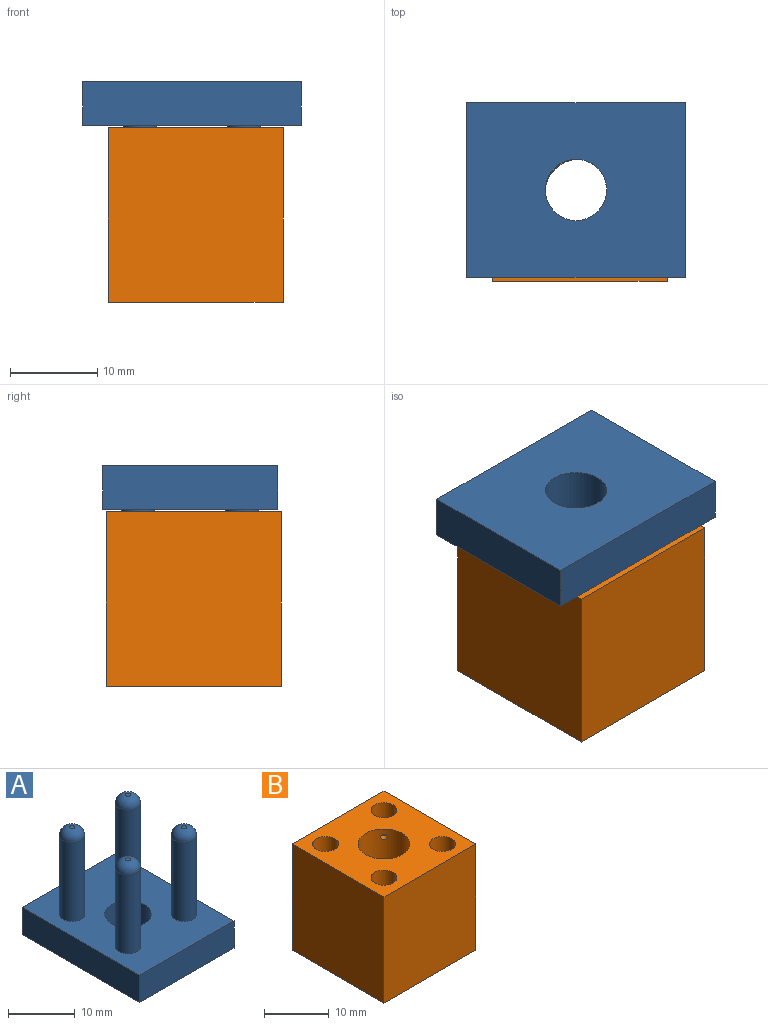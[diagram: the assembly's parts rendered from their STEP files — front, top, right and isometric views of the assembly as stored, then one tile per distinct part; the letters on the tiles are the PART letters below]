
ASSEMBLY  parts=2 mates=1
PART A: 19 faces, bbox 20x25x21 mm
  f0: plane 20x5mm, normal (0,1,0), area 100mm2, adj f1,f4,f5,f6
  f1: plane 25x5mm, normal (-1,0,0), area 125mm2, adj f0,f2,f5,f6
  f2: plane 20x5mm, normal (0,-1,0), area 100mm2, adj f1,f4,f5,f6
  f3: cylinder r=3.5mm len=7mm, axis (0,0,1), area 110mm2, adj f5,f6
  f4: plane 25x5mm, normal (1,0,0), area 125mm2, adj f0,f2,f5,f6
  f5: plane 25x20mm, normal (0,0,-1), area 461.5mm2, adj f0,f1,f2,f3,f4
  f6: plane 25x20mm, normal (0,0,1), area 416.2mm2, adj f0,f1,f2,f3,f4,f7,f9,f11
  f7: cylinder r=1.9mm len=14.5mm, axis (0,0,-1), area 173.1mm2, adj f6,f17
  f8: plane 0.8x0.8mm, normal (0,0,1), area 0.5mm2, adj f17
  f9: cylinder r=1.9mm len=14.5mm, axis (0,0,-1), area 173.1mm2, adj f6,f18
  f10: plane 0.8x0.8mm, normal (0,0,1), area 0.5mm2, adj f18
  f11: cylinder r=1.9mm len=14.5mm, axis (0,0,-1), area 173.1mm2, adj f6,f15
  f12: plane 0.8x0.8mm, normal (0,0,1), area 0.5mm2, adj f15
  f13: cylinder r=1.9mm len=14.5mm, axis (0,0,-1), area 173.1mm2, adj f6,f16
  f14: plane 0.8x0.8mm, normal (0,0,1), area 0.5mm2, adj f16
  f15: torus R=0.4mm, axis (0,0,1), area 20.1mm2, adj f11,f12
  f16: torus R=0.4mm, axis (0,0,1), area 20.1mm2, adj f13,f14
  f17: torus R=0.4mm, axis (0,0,1), area 20.1mm2, adj f7,f8
  f18: torus R=0.4mm, axis (0,0,1), area 20.1mm2, adj f9,f10
PART B: 61 faces, bbox 20x20x20 mm
  f0: plane 0.35x0.35mm, normal (0,0,1), area 0mm2, adj f1,f2
  f1: cylinder r=0.5mm len=3.54mm, axis (0.71,0.71,0), area 10.7mm2, adj f0,f2,f3,f4,f5
  f2: cylinder r=0.5mm len=16.75mm, axis (0,0,1), area 51.3mm2, adj f0,f1,f3,f6,f7
  f3: plane 0.35x0.35mm, normal (0,0,1), area 0mm2, adj f1,f2
  f4: plane 1x0.71mm, normal (0.71,0.71,0), area 0.8mm2, adj f1
  f5: cylinder r=0.5mm len=1mm, axis (0,0,1), area 1mm2, adj f1
  f6: cylinder r=0.5mm len=0.71mm, axis (-0.71,-0.71,0), area 0.2mm2, adj f2,f7,f8
  f7: cylinder r=0.5mm len=2.14mm, axis (-0.71,-0.71,0), area 5.2mm2, adj f2,f6,f8,f9
  f8: plane 1x0.71mm, normal (-0.71,-0.71,0), area 0.8mm2, adj f6,f7
  f9: cylinder r=4mm len=20mm, axis (0,0,-1), area 499.5mm2, adj f7,f10,f11,f12,f13,f14
  f10: plane 20x20mm, normal (0,0,1), area 299.5mm2, adj f9,f15,f16,f17,f18,f19,f20,f21
  f11: plane 20x20mm, normal (0,0,-1), area 349.7mm2, adj f9,f19,f20,f21,f22
  f12: cylinder r=0.5mm len=2.14mm, axis (-0.71,0.71,0), area 5.3mm2, adj f9,f23,f24,f25
  f13: cylinder r=0.5mm len=2.14mm, axis (0.71,-0.71,0), area 5.2mm2, adj f9,f26,f27,f28
  f14: cylinder r=0.5mm len=2.14mm, axis (0.71,0.71,0), area 5.2mm2, adj f9,f29,f30,f31
  f15: cylinder r=2mm len=14.5mm, axis (0,0,-1), area 182.2mm2, adj f10,f32
  f16: cylinder r=2mm len=14.5mm, axis (0,0,-1), area 182.2mm2, adj f10,f33
  f17: cylinder r=2mm len=14.5mm, axis (0,0,-1), area 182.2mm2, adj f10,f34
  f18: cylinder r=2mm len=14.5mm, axis (0,0,-1), area 182.2mm2, adj f10,f35
  f19: plane 20x20mm, normal (1,0,0), area 400mm2, adj f10,f11,f20,f22
  f20: plane 20x20mm, normal (0,1,0), area 400mm2, adj f10,f11,f19,f21
  f21: plane 20x20mm, normal (-1,0,0), area 400mm2, adj f10,f11,f20,f22
  f22: plane 20x20mm, normal (0,-1,0), area 400mm2, adj f10,f11,f19,f21
  f23: cylinder r=0.5mm len=0.71mm, axis (-0.71,0.71,0), area 0.1mm2, adj f12,f24,f25
  f24: plane 1x0.71mm, normal (-0.71,0.71,0), area 0.8mm2, adj f12,f23
  f25: cylinder r=0.5mm len=16.75mm, axis (0,0,1), area 51.3mm2, adj f12,f23,f36,f37,f38
  f26: cylinder r=0.5mm len=0.71mm, axis (0.71,-0.71,0), area 0.1mm2, adj f13,f27,f28
  f27: plane 1x0.71mm, normal (0.71,-0.71,0), area 0.8mm2, adj f13,f26
  f28: cylinder r=0.5mm len=16.75mm, axis (0,0,1), area 51.3mm2, adj f13,f26,f39,f40,f41,f42
  f29: cylinder r=0.5mm len=0.71mm, axis (0.71,0.71,0), area 0.1mm2, adj f14,f30,f31
  f30: plane 1x0.71mm, normal (0.71,0.71,0), area 0.8mm2, adj f14,f29
  f31: cylinder r=0.5mm len=16.75mm, axis (0,0,1), area 51.3mm2, adj f14,f29,f43,f44,f45,f46
  f32: torus R=0.5mm, axis (0,0,1), area 21.5mm2, adj f15,f47
  f33: torus R=0.5mm, axis (0,0,1), area 21.5mm2, adj f16,f48
  f34: torus R=0.5mm, axis (0,0,1), area 21.5mm2, adj f17,f49
  f35: torus R=0.5mm, axis (0,0,1), area 21.5mm2, adj f18,f50
  f36: plane 0.35x0.35mm, normal (0,0,1), area 0mm2, adj f25,f37
  f37: cylinder r=0.5mm len=3.54mm, axis (0.71,-0.71,0), area 10.7mm2, adj f25,f36,f38,f51,f52
  f38: plane 0.35x0.35mm, normal (0,0,1), area 0mm2, adj f25,f37
  f39: plane 0.35x0.35mm, normal (0,0,1), area 0mm2, adj f28,f40
  f40: cylinder r=0.5mm len=3.54mm, axis (-0.71,0.71,0), area 10.6mm2, adj f28,f39,f41,f42,f50,f53,f54
  f41: plane 0.35x0.35mm, normal (0,0,1), area 0mm2, adj f28,f40
  f42: cylinder r=0.5mm len=0.48mm, axis (-0.71,0.71,0), area 0.1mm2, adj f28,f40,f54
  f43: cylinder r=0.5mm len=0.48mm, axis (-0.71,-0.71,0), area 0.1mm2, adj f31,f44,f55
  f44: cylinder r=0.5mm len=3.54mm, axis (-0.71,-0.71,0), area 10.7mm2, adj f31,f43,f45,f46,f47,f55,f56
  f45: plane 0.35x0.35mm, normal (0,0,1), area 0mm2, adj f31,f44
  f46: plane 0.35x0.35mm, normal (0,0,1), area 0mm2, adj f31,f44
  f47: cylinder r=0.5mm len=3mm, axis (0,0,1), area 8.4mm2, adj f32,f44,f56,f57
  f48: cylinder r=0.5mm len=3mm, axis (0,0,1), area 9.4mm2, adj f33,f58
  f49: cylinder r=0.5mm len=3mm, axis (0,0,1), area 9.4mm2, adj f34,f59
  f50: cylinder r=0.5mm len=3mm, axis (0,0,1), area 8.4mm2, adj f35,f40,f53,f60
  f51: plane 1x0.71mm, normal (0.71,-0.71,0), area 0.8mm2, adj f37
  f52: cylinder r=0.5mm len=1mm, axis (0,0,1), area 1mm2, adj f37
  f53: cylinder r=0.5mm len=0.35mm, axis (0,0,1), area 0mm2, adj f40,f50,f60
  f54: plane 1x0.71mm, normal (-0.71,0.71,0), area 0.8mm2, adj f40,f42
  f55: plane 1x0.71mm, normal (-0.71,-0.71,0), area 0.8mm2, adj f43,f44
  f56: cylinder r=0.5mm len=0.35mm, axis (0,0,1), area 0mm2, adj f44,f47,f57
  f57: plane 1x1mm, normal (0,0,1), area 0.8mm2, adj f47,f56
  f58: plane 1x1mm, normal (0,0,1), area 0.8mm2, adj f48
  f59: plane 1x1mm, normal (0,0,1), area 0.8mm2, adj f49
  f60: plane 1x1mm, normal (0,0,1), area 0.8mm2, adj f50,f53
PLACE A rot(axis=(0.71,-0.71,0),180deg) t=(24.67,-4.38,10.26)mm
PLACE B t=(25.09,-4.8,0)mm fixed
MATE slider A.f7 <-> B.f18  axis (0,0,1) through (18.73,1.56,3.01)mm
